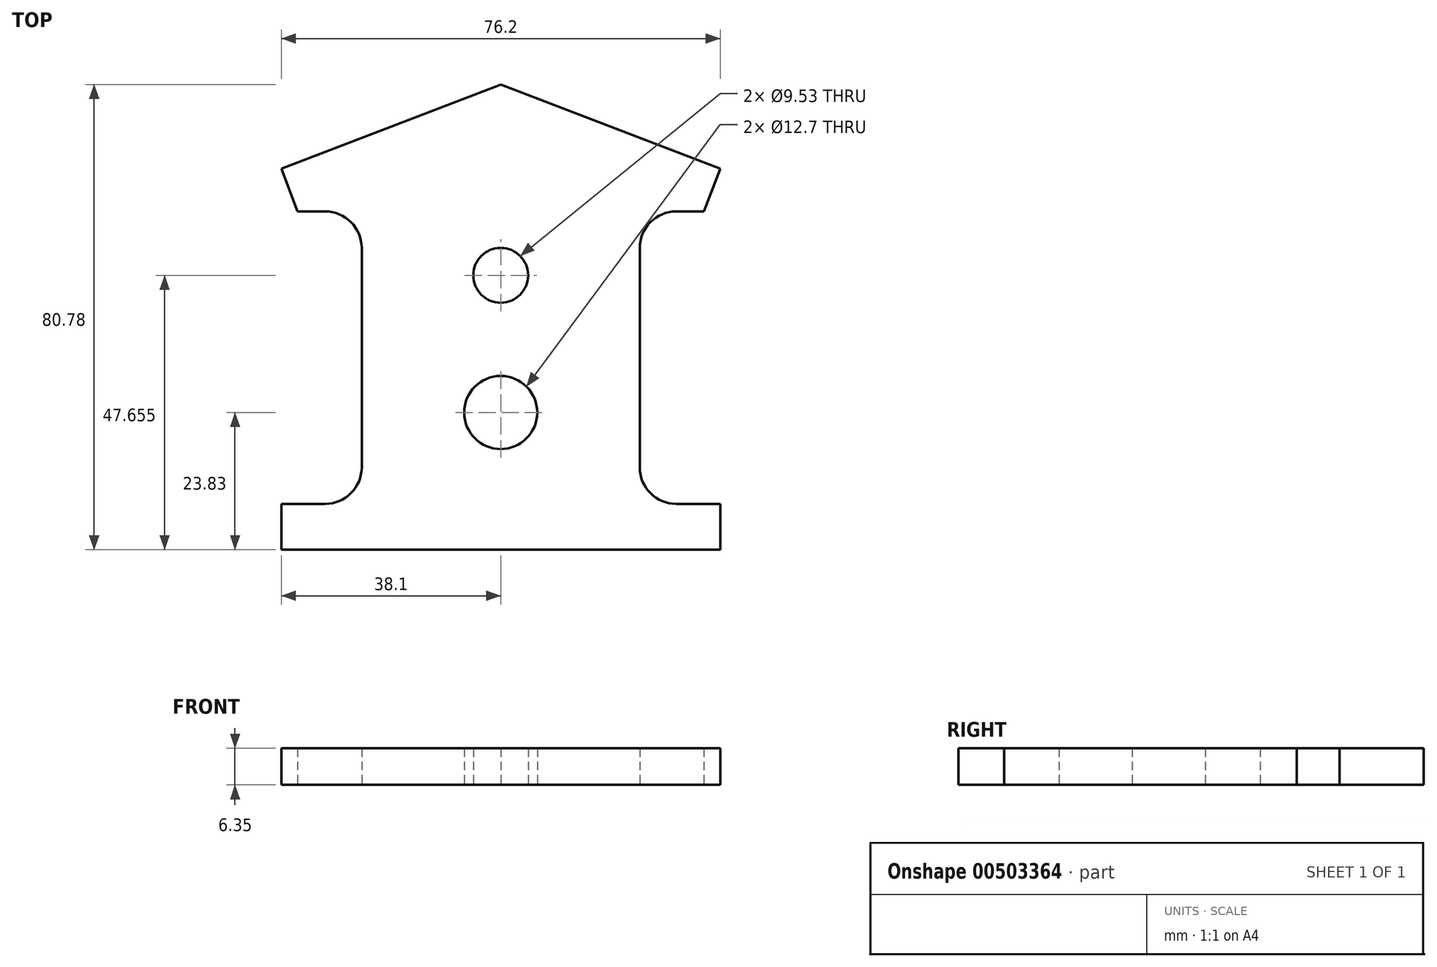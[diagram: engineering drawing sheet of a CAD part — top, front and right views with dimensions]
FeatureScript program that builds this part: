
annotation { "Feature Type Name" : "Feature", "Feature Type Description" : "" }
export const myFeature = defineFeature(function(context is Context, id is Id, definition is map)
    precondition{}
    {
        {
            var Q0;
            Q0=qCreatedBy(makeId("Top.planeOp"),FACE);
            var sketch = newSketch(context, id + "F0", { "sketchPlane" : qUnion([Q0])});
            skLineSegment(sketch, "E0.top", {"start": v(-38.1, -23.83) * mm, "end": v(38.1, -23.83) * mm});
            skLineSegment(sketch, "E0.left", {"start": v(-38.1, -15.88) * mm, "end": v(-38.1, -23.83) * mm});
            skLineSegment(sketch, "E1", {"start": v(0, 56.95) * mm, "end": v(-38.1, 42.32) * mm});
            skLineSegment(sketch, "E2.MirrorCS", {"start": v(0, 56.95) * mm, "end": v(38.1, 42.32) * mm});
            skLineSegment(sketch, "E3", {"start": v(-38.1, -15.88) * mm, "end": v(-30.48, -15.88) * mm});
            skLineSegment(sketch, "E4", {"start": v(-24.13, -9.52) * mm, "end": v(-24.13, 28.58) * mm});
            skLineSegment(sketch, "E5", {"start": v(-30.48, 34.93) * mm, "end": v(-35.26, 34.93) * mm});
            skLineSegment(sketch, "E6", {"start": v(-38.1, 42.32) * mm, "end": v(-35.26, 34.93) * mm});
            skPoint(sketch, "E7.visualSharp", {"position": v(-24.13, 34.93) * mm});
            skArc(sketch, "E7.filletArc", {"start": v(-24.13, 28.58) * mm, "mid": v(-25.99, 33.07) * mm, "end": v(-30.48, 34.93) * mm});
            skPoint(sketch, "E8.visualSharp", {"position": v(-24.13, -15.88) * mm});
            skArc(sketch, "E8.filletArc", {"start": v(-30.48, -15.88) * mm, "mid": v(-25.99, -14.02) * mm, "end": v(-24.13, -9.52) * mm});
            skLineSegment(sketch, "E9.MirrorCS", {"start": v(38.1, 42.32) * mm, "end": v(35.26, 34.93) * mm});
            skLineSegment(sketch, "E10.MirrorCS", {"start": v(30.48, 34.93) * mm, "end": v(35.26, 34.93) * mm});
            skArc(sketch, "E11.MirrorCS", {"start": v(24.13, 28.58) * mm, "mid": v(25.99, 33.07) * mm, "end": v(30.48, 34.93) * mm});
            skLineSegment(sketch, "E12.MirrorCS", {"start": v(24.13, -9.52) * mm, "end": v(24.13, 28.58) * mm});
            skArc(sketch, "E13.MirrorCS", {"start": v(30.48, -15.88) * mm, "mid": v(25.99, -14.02) * mm, "end": v(24.13, -9.52) * mm});
            skLineSegment(sketch, "E14.MirrorCS", {"start": v(38.1, -15.88) * mm, "end": v(30.48, -15.88) * mm});
            skLineSegment(sketch, "E15.MirrorCS", {"start": v(38.1, -15.88) * mm, "end": v(38.1, -23.83) * mm});
            skSolve(sketch);
        }
        {
            var Q0;
            Q0 = qSketchRegion(id + "F0", true);
            extrude(context, id + "F1", {"entities" : qUnion([Q0]), "depth" : 6.35 * mm});
        }
        {
            var Q0;
            Q0=qCreatedBy(makeId("Top.planeOp"),FACE);
            var sketch = newSketch(context, id + "F2", { "sketchPlane" : qUnion([Q0])});
            skCircle(sketch, "E16", {"center": v(0, 0) * mm, "radius": 6.35 * mm});
            skCircle(sketch, "E17", {"center": v(0, 23.83) * mm, "radius": 4.76 * mm});
            skSolve(sketch);
        }
        {
            var Q0;
            Q0 = qSketchRegion(id + "F2", true);
            extrude(context, id + "F3", {"entities" : qUnion([Q0]), "operationType" : NewBodyOperationType.REMOVE, "endBound" : BoundingType.THROUGH_ALL, "depth" : 6.35 * mm});
        }
    });
